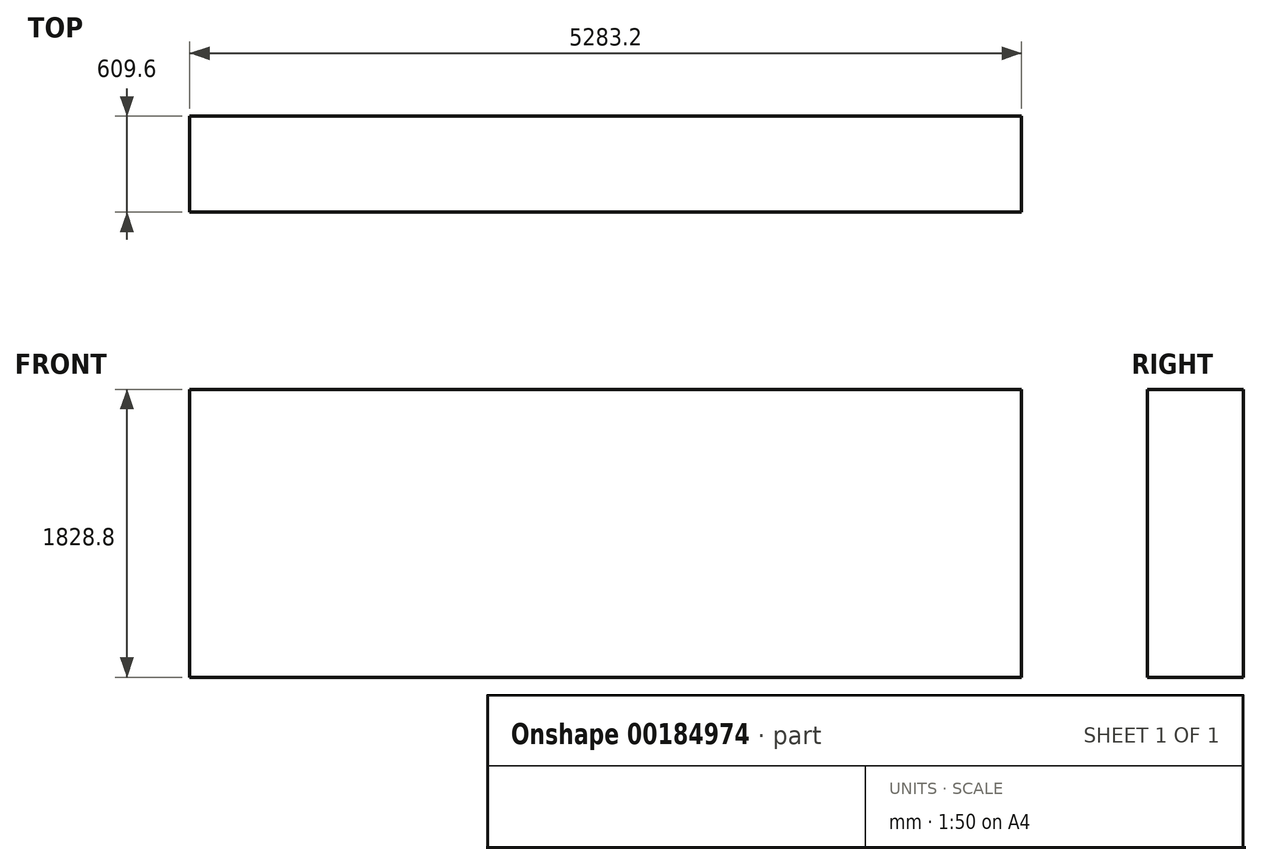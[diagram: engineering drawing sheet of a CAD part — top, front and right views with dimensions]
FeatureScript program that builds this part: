
annotation { "Feature Type Name" : "Feature", "Feature Type Description" : "" }
export const myFeature = defineFeature(function(context is Context, id is Id, definition is map)
    precondition{}
    {
        {
            var Q0;
            Q0=qCreatedBy(makeId("Top.planeOp"),FACE);
            var sketch = newSketch(context, id + "F0", { "sketchPlane" : qUnion([Q0])});
            skLineSegment(sketch, "E0.bottom", {"start": v(2641.6, 304.8) * mm, "end": v(-2641.6, 304.8) * mm});
            skLineSegment(sketch, "E0.top", {"start": v(2641.6, -304.8) * mm, "end": v(-2641.6, -304.8) * mm});
            skLineSegment(sketch, "E0.left", {"start": v(2641.6, 304.8) * mm, "end": v(2641.6, -304.8) * mm});
            skLineSegment(sketch, "E0.right", {"start": v(-2641.6, 304.8) * mm, "end": v(-2641.6, -304.8) * mm});
            skPoint(sketch, "E0.middle", {"position": v(0, 0) * mm});
            skSolve(sketch);
        }
        {
            var Q0;
            Q0=makeQuery(id+"F0.imprint","IMPRINT",FACE,{"disambiguationData":[TD([[makeQuery(id+"F0.imprint","IMPRINT",EDGE,{"derivedFrom":sQuery(id+"F0.wireOp",EDGE,"E0.bottom")}),1.0]])]});
            extrude(context, id + "F1", {"entities" : qUnion([Q0]), "depth" : 1828.8 * mm});
        }
    });
